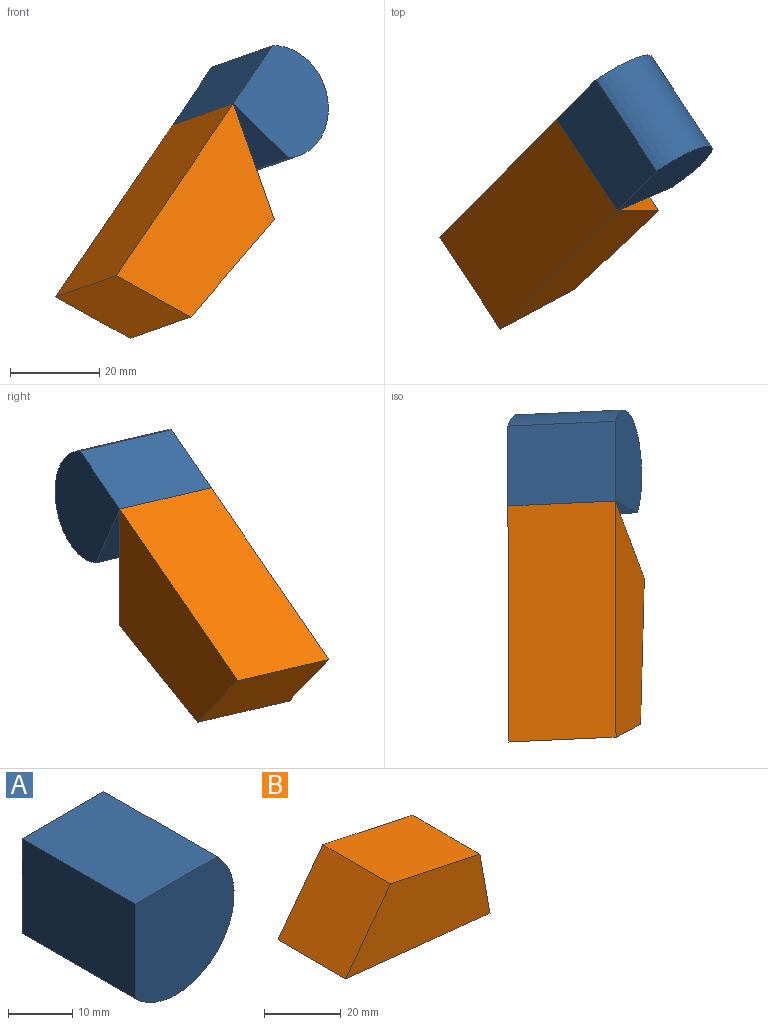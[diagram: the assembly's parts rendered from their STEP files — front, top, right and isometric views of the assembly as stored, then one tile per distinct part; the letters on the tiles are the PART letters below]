
ASSEMBLY  parts=2 mates=2
PART A: 5 faces, bbox 21.8x25x21.8 mm
  f0: plane 25x18.08mm, normal (0,0,1), area 452.1mm2, adj f1,f2,f3,f4
  f1: plane 25x18.08mm, normal (-1,0,0), area 452.1mm2, adj f0,f2,f3,f4
  f2: cylinder r=12.79mm len=25mm, axis (0,1,0), area 1004.3mm2, adj f0,f1,f3,f4
  f3: plane 21.83x21.83mm, normal (0,-1,0), area 420.4mm2, adj f0,f1,f2
  f4: plane 21.83x21.83mm, normal (0,1,0), area 420.4mm2, adj f0,f1,f2
PART B: 6 faces, bbox 53.2x25x27.7 mm
  f0: plane 32.91x25mm, normal (0.21,0,0.98), area 840.9mm2, adj f1,f3,f4,f5
  f1: plane 25x22.09mm, normal (-0.8,0,0.6), area 690.4mm2, adj f0,f2,f4,f5
  f2: plane 53.21x25mm, normal (-0.1,0,-0.99), area 1337.5mm2, adj f1,f3,f4,f5
  f3: plane 25x20.73mm, normal (0.98,0,0.18), area 526.5mm2, adj f0,f2,f4,f5
  f4: plane 53.21x27.69mm, normal (0,-1,0), area 962.2mm2, adj f0,f1,f2,f3
  f5: plane 53.21x27.69mm, normal (0,1,0), area 962.2mm2, adj f0,f1,f2,f3
PLACE A rot(axis=(0.06,-0.8,0.59),60.8deg) t=(16.83,104.96,149.25)mm
PLACE B rot(axis=(-0.33,0.94,0.05),126.4deg) t=(-215.74,-90.11,-23.96)mm
MATE fastened B.f4 <-> B.f2  axis (-0.54,0.82,-0.19) through (-77.39,-4.5,79.73)mm
MATE fastened A.f0 <-> B.f2  axis (-0.68,-0.3,0.67) through (-77.39,-4.5,79.73)mm
